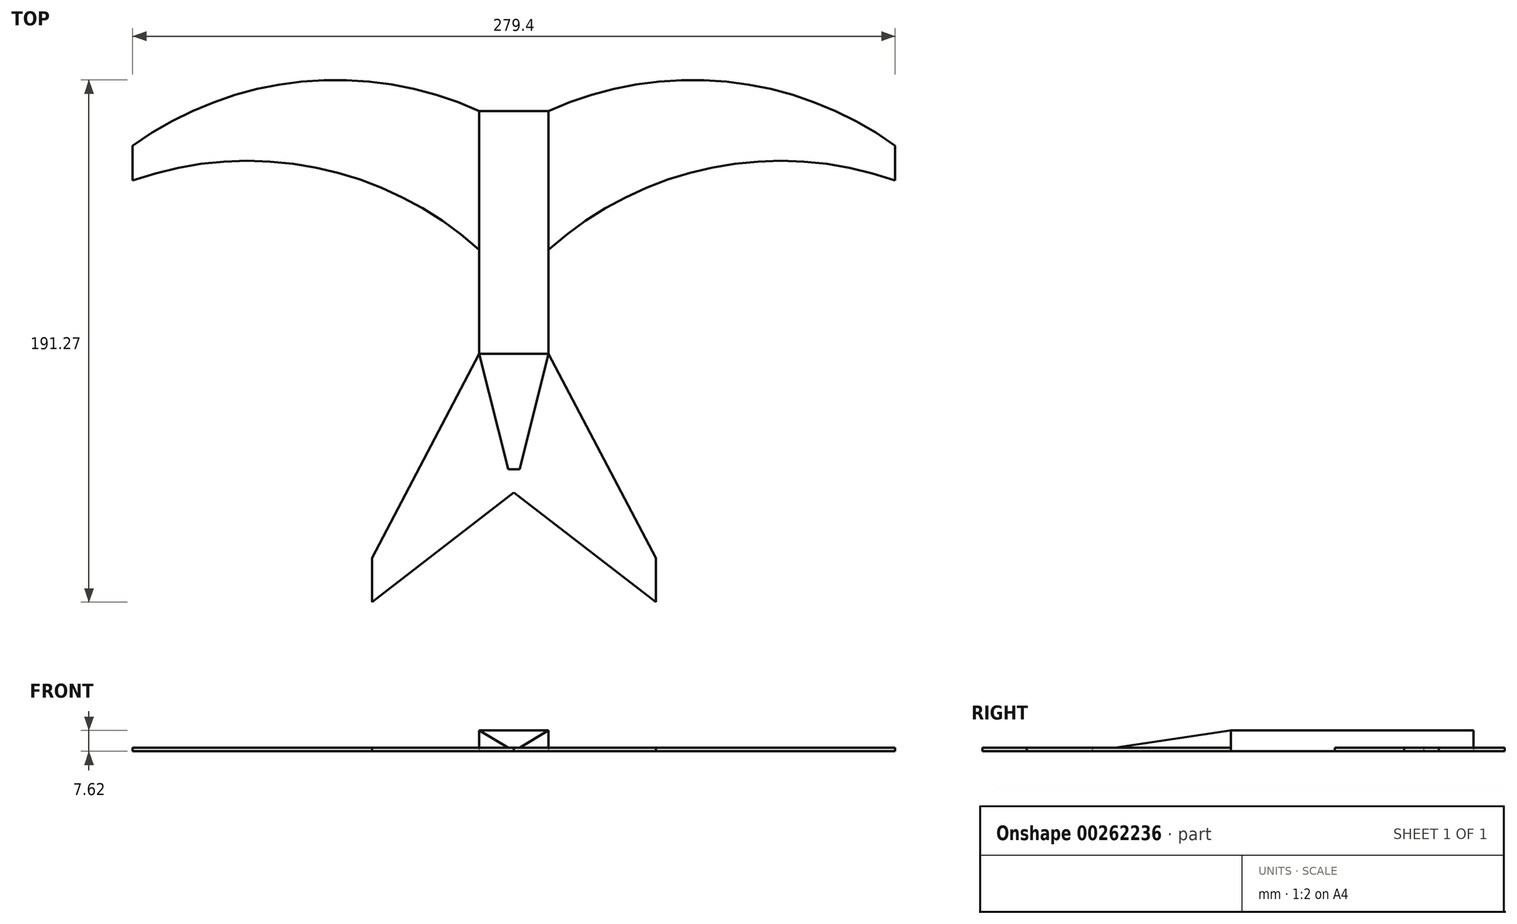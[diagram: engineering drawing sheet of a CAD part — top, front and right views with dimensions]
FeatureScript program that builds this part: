
annotation { "Feature Type Name" : "Feature", "Feature Type Description" : "" }
export const myFeature = defineFeature(function(context is Context, id is Id, definition is map)
    precondition{}
    {
        {
            var Q0;
            Q0=qCreatedBy(makeId("Top.planeOp"),FACE);
            var sketch = newSketch(context, id + "F0", { "sketchPlane" : qUnion([Q0])});
            skArc(sketch, "E0", {"start": v(-12.7, 12.7) * mm, "mid": v(-77.91, 23.46) * mm, "end": v(-139.7, 0) * mm});
            skLineSegment(sketch, "E1.bottom", {"start": v(-12.7, 12.7) * mm, "end": v(12.7, 12.7) * mm});
            skLineSegment(sketch, "E1.top", {"start": v(-12.7, -76.2) * mm, "end": v(12.7, -76.2) * mm});
            skLineSegment(sketch, "E1.left", {"start": v(-12.7, 12.7) * mm, "end": v(-12.7, -76.2) * mm});
            skLineSegment(sketch, "E1.right", {"start": v(12.7, 12.7) * mm, "end": v(12.7, -76.2) * mm});
            skArc(sketch, "E2", {"start": v(139.7, 0) * mm, "mid": v(77.91, 23.46) * mm, "end": v(12.7, 12.7) * mm});
            skLineSegment(sketch, "E3", {"start": v(-139.7, 0) * mm, "end": v(-139.7, -12.7) * mm});
            skArc(sketch, "E4", {"start": v(-12.7, -38.1) * mm, "mid": v(-72.72, -8) * mm, "end": v(-139.7, -12.7) * mm});
            skLineSegment(sketch, "E5", {"start": v(139.7, 0) * mm, "end": v(139.7, -12.7) * mm});
            skArc(sketch, "E6", {"start": v(139.7, -12.7) * mm, "mid": v(72.72, -8) * mm, "end": v(12.7, -38.1) * mm});
            skLineSegment(sketch, "E7", {"start": v(-12.7, -76.2) * mm, "end": v(0, -127) * mm});
            skLineSegment(sketch, "E8", {"start": v(0, -127) * mm, "end": v(12.7, -76.2) * mm});
            skSolve(sketch);
        }
        {
            var Q0;
            {var subQ3=sQuery(id+"F0.wireOp",EDGE,"E1.bottom");Q0=makeQuery(id+"F0.imprint","IMPRINT",FACE,{"disambiguationData":[TD([[makeQuery(id+"F0.imprint","IMPRINT",EDGE,{"derivedFrom":subQ3}),-1.0]])]});}
            var Q1;
            Q1=makeQuery(id+"F0.imprint","IMPRINT",FACE,{"disambiguationData":[TD([[makeQuery(id+"F0.imprint","IMPRINT",EDGE,{"derivedFrom":sQuery(id+"F0.wireOp",EDGE,"E1.top")}),-1.0]])]});
            extrude(context, id + "F1", {"entities" : qUnion([Q0, Q1]), "depth" : 7.62 * mm});
        }
        {
            var Q0;
            {var subQ0=sQuery(id+"F0.wireOp",EDGE,"E2");Q0=makeQuery(id+"F0.imprint","IMPRINT",FACE,{"disambiguationData":[TD([[makeQuery(id+"F0.imprint","IMPRINT",EDGE,{"derivedFrom":subQ0}),1.0]])]});}
            var Q1;
            {var subQ0=sQuery(id+"F0.wireOp",EDGE,"E0");Q1=makeQuery(id+"F0.imprint","IMPRINT",FACE,{"disambiguationData":[TD([[makeQuery(id+"F0.imprint","IMPRINT",EDGE,{"derivedFrom":subQ0}),1.0]])]});}
            extrude(context, id + "F2", {"entities" : qUnion([Q0, Q1]), "operationType" : NewBodyOperationType.ADD, "depth" : 1.27 * mm});
        }
        {
            var Q0;
            Q0=qCreatedBy(makeId("Front.planeOp"),FACE);
            cPlane(context, id + "F3", {"entities" : qUnion([Q0]), "cplaneType" : CPlaneType.OFFSET, "offset" : 76.2 * mm, "width" : 152.4 * mm, "height" : 152.4 * mm});
        }
        {
            var Q0;
            Q0=qCreatedBy(id+"F3.planeOp",FACE);
            var sketch = newSketch(context, id + "F4", { "sketchPlane" : qUnion([Q0])});
            skLineSegment(sketch, "E9.bottom", {"start": v(25.4, 7.62) * mm, "end": v(-25.4, 7.62) * mm});
            skLineSegment(sketch, "E9.top", {"start": v(25.4, 26.69) * mm, "end": v(-25.4, 26.69) * mm});
            skLineSegment(sketch, "E9.left", {"start": v(25.4, 7.62) * mm, "end": v(25.4, 26.69) * mm});
            skLineSegment(sketch, "E9.right", {"start": v(-25.4, 7.62) * mm, "end": v(-25.4, 26.69) * mm});
            skSolve(sketch);
        }
        {
            var Q0;
            Q0=qCreatedBy(id+"F3.planeOp",FACE);
            cPlane(context, id + "F5", {"entities" : qUnion([Q0]), "cplaneType" : CPlaneType.OFFSET, "offset" : 50.8 * mm, "width" : 152.4 * mm, "height" : 152.4 * mm});
        }
        {
            var Q0;
            Q0=qCreatedBy(id+"F5.planeOp",FACE);
            var sketch = newSketch(context, id + "F6", { "sketchPlane" : qUnion([Q0])});
            skLineSegment(sketch, "E10.bottom", {"start": v(29.83, 0) * mm, "end": v(-29.63, 0) * mm});
            skLineSegment(sketch, "E10.top", {"start": v(29.83, 29.44) * mm, "end": v(-29.63, 29.44) * mm});
            skLineSegment(sketch, "E10.left", {"start": v(29.83, 0) * mm, "end": v(29.83, 29.44) * mm});
            skLineSegment(sketch, "E10.right", {"start": v(-29.63, 0) * mm, "end": v(-29.63, 29.44) * mm});
            skSolve(sketch);
        }
        {
            var Q1;
            Q1=makeQuery(id+"F4.imprint","IMPRINT",FACE,{"disambiguationData":[TD([[makeQuery(id+"F4.imprint","IMPRINT",EDGE,{"derivedFrom":sQuery(id+"F4.wireOp",EDGE,"E9.bottom")}),-1.0]])]});
            var Q2;
            Q2=makeQuery(id+"F6.imprint","IMPRINT",FACE,{"disambiguationData":[TD([[makeQuery(id+"F6.imprint","IMPRINT",EDGE,{"derivedFrom":sQuery(id+"F6.wireOp",EDGE,"E10.bottom")}),-1.0]])]});
            loft(context, id + "F7", {"operationType" : NewBodyOperationType.REMOVE, "sheetProfilesArray" : [{ "sheetProfileEntities" : qUnion([Q1]) }, { "sheetProfileEntities" : qUnion([Q2]) }]});
        }
        {
            var Q0;
            Q0=makeQuery(id+"F0.imprint","IMPRINT",FACE,{"disambiguationData":[TD([[makeQuery(id+"F0.imprint","IMPRINT",EDGE,{"derivedFrom":sQuery(id+"F0.wireOp",EDGE,"E1.top")}),-1.0]])]});
            var sketch = newSketch(context, id + "F8", { "sketchPlane" : qUnion([Q0])});
            skLineSegment(sketch, "E11.0.0", {"start": v(12.7, -76.2) * mm, "end": v(12.7, -38.1) * mm});
            skLineSegment(sketch, "E11.0.1", {"start": v(12.7, -38.1) * mm, "end": v(12.7, 12.7) * mm});
            skLineSegment(sketch, "E11.0.2", {"start": v(12.7, 12.7) * mm, "end": v(-12.7, 12.7) * mm});
            skLineSegment(sketch, "E11.0.3", {"start": v(-12.7, 12.7) * mm, "end": v(-12.7, -38.1) * mm});
            skLineSegment(sketch, "E11.0.4", {"start": v(-12.7, -38.1) * mm, "end": v(-12.7, -76.2) * mm});
            skLineSegment(sketch, "E11.0.5", {"start": v(-12.7, -76.2) * mm, "end": v(12.7, -76.2) * mm});
            skLineSegment(sketch, "E12.0.0", {"start": v(12.7, -76.2) * mm, "end": v(-12.7, -76.2) * mm});
            skLineSegment(sketch, "E13.0.0", {"start": v(139.7, -12.7) * mm, "end": v(139.7, 0) * mm});
            skArc(sketch, "E13.0.1", {"start": v(139.7, 0) * mm, "mid": v(77.91, 23.46) * mm, "end": v(12.7, 12.7) * mm});
            skLineSegment(sketch, "E13.0.2", {"start": v(12.7, 12.7) * mm, "end": v(12.7, -38.1) * mm});
            skArc(sketch, "E13.0.3", {"start": v(12.7, -38.1) * mm, "mid": v(72.72, -8) * mm, "end": v(139.7, -12.7) * mm});
            skLineSegment(sketch, "E14.0.0", {"start": v(-12.7, -38.1) * mm, "end": v(-12.7, 12.7) * mm});
            skArc(sketch, "E14.0.1", {"start": v(-12.7, 12.7) * mm, "mid": v(-77.91, 23.46) * mm, "end": v(-139.7, 0) * mm});
            skLineSegment(sketch, "E14.0.2", {"start": v(-139.7, 0) * mm, "end": v(-139.7, -12.7) * mm});
            skArc(sketch, "E14.0.3", {"start": v(-139.7, -12.7) * mm, "mid": v(-72.72, -8) * mm, "end": v(-12.7, -38.1) * mm});
            skPoint(sketch, "E15.end.orphan", {"position": v(0, -127.44) * mm});
            skLineSegment(sketch, "E16", {"start": v(12.7, -76.2) * mm, "end": v(52, -151.02) * mm});
            skLineSegment(sketch, "E17", {"start": v(52, -151.02) * mm, "end": v(52, -167.18) * mm});
            skLineSegment(sketch, "E18", {"start": v(52, -167.18) * mm, "end": v(0, -127) * mm});
            skPoint(sketch, "E19.endSnap0", {"position": v(0, -76.2) * mm});
            skLineSegment(sketch, "E20.MirrorCS", {"start": v(-12.7, -76.2) * mm, "end": v(-52, -151.02) * mm});
            skLineSegment(sketch, "E21.MirrorCS", {"start": v(-52, -151.02) * mm, "end": v(-52, -167.18) * mm});
            skLineSegment(sketch, "E22.MirrorCS", {"start": v(-52, -167.18) * mm, "end": v(0, -127) * mm});
            skPoint(sketch, "E19.end.orphan", {"position": v(0, -58) * mm});
            skSolve(sketch);
        }
        {
            var Q0;
            Q0=makeQuery(id+"F0.imprint","IMPRINT",FACE,{"disambiguationData":[TD([[makeQuery(id+"F0.imprint","IMPRINT",EDGE,{"derivedFrom":sQuery(id+"F0.wireOp",EDGE,"E1.top")}),-1.0]])]});
            var Q1;
            Q1=makeQuery(id+"F8.imprint","IMPRINT",FACE,{"disambiguationData":[TD([[makeQuery(id+"F8.imprint","IMPRINT",EDGE,{"derivedFrom":sQuery(id+"F8.wireOp",EDGE,"E20.MirrorCS")}),1.0]])]});
            var Q2;
            Q2=makeQuery(id+"F8.imprint","IMPRINT",FACE,{"disambiguationData":[TD([[makeQuery(id+"F8.imprint","IMPRINT",EDGE,{"derivedFrom":sQuery(id+"F8.wireOp",EDGE,"E16")}),-1.0]])]});
            extrude(context, id + "F9", {"entities" : qUnion([Q0, Q1, Q2]), "operationType" : NewBodyOperationType.ADD, "depth" : 1.27 * mm});
        }
    });
